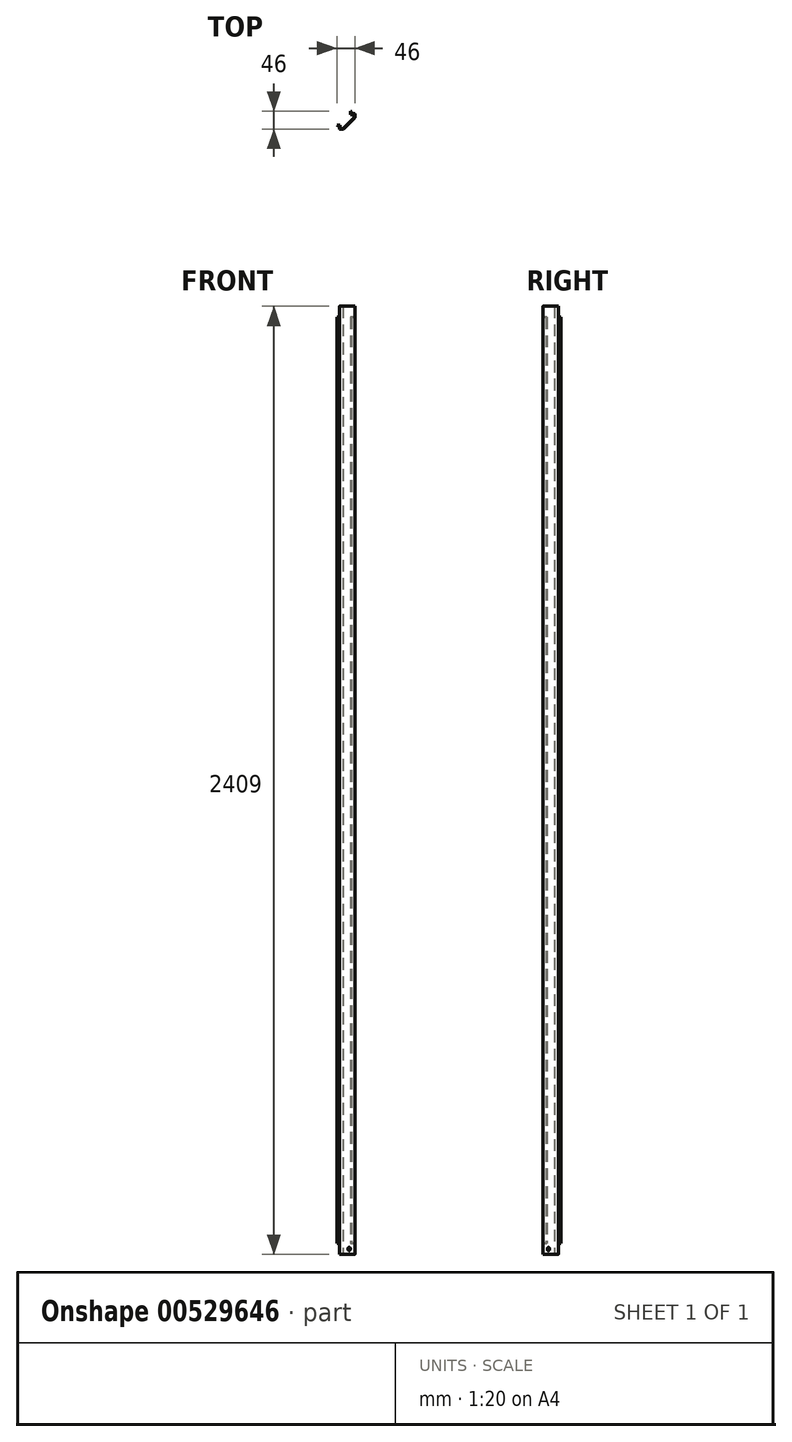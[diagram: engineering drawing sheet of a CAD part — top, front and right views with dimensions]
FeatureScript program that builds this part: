
annotation { "Feature Type Name" : "Feature", "Feature Type Description" : "" }
export const myFeature = defineFeature(function(context is Context, id is Id, definition is map)
    precondition{}
    {
        {
            var Q0;
            Q0=qCreatedBy(makeId("Top.planeOp"),FACE);
            var sketch = newSketch(context, id + "F0", { "sketchPlane" : qUnion([Q0])});
            skLineSegment(sketch, "E0", {"start": v(-68.1, 0) * mm, "end": v(72.16, 0) * mm, "construction": true});
            skLineSegment(sketch, "E1", {"start": v(0, 70.28) * mm, "end": v(0, -61.88) * mm, "construction": true});
            skLineSegment(sketch, "E2.bottom", {"start": v(-19.75, 19.75) * mm, "end": v(19.75, 19.75) * mm, "construction": true});
            skLineSegment(sketch, "E2.top", {"start": v(-19.75, -19.75) * mm, "end": v(19.75, -19.75) * mm, "construction": true});
            skLineSegment(sketch, "E2.left", {"start": v(-19.75, 19.75) * mm, "end": v(-19.75, -19.75) * mm, "construction": true});
            skLineSegment(sketch, "E2.right", {"start": v(19.75, 19.75) * mm, "end": v(19.75, -19.75) * mm, "construction": true});
            skLineSegment(sketch, "E3", {"start": v(-19.75, -19.75) * mm, "end": v(-9.25, -19.75) * mm});
            skLineSegment(sketch, "E4", {"start": v(19.75, 19.75) * mm, "end": v(19.75, 9.25) * mm});
            skLineSegment(sketch, "E5", {"start": v(-9.25, -19.75) * mm, "end": v(19.75, 9.25) * mm});
            skLineSegment(sketch, "E6.0", {"start": v(-19.75, -17.75) * mm, "end": v(-10.08, -17.75) * mm});
            skLineSegment(sketch, "E6.1", {"start": v(-10.08, -17.75) * mm, "end": v(17.75, 10.08) * mm});
            skLineSegment(sketch, "E6.2", {"start": v(17.75, 19.75) * mm, "end": v(17.75, 10.08) * mm});
            skLineSegment(sketch, "E7", {"start": v(-19.75, -19.75) * mm, "end": v(-19.75, -17.75) * mm});
            skLineSegment(sketch, "E8", {"start": v(19.75, 19.75) * mm, "end": v(17.75, 19.75) * mm});
            skSolve(sketch);
        }
        {
            var Q0;
            Q0=qSketchRegion(id+"F0",true);
            extrude(context, id + "F1", {"entities" : qUnion([Q0]), "depth" : 28 * mm});
        }
        {
            var Q0;
            Q0=makeQuery(id+"F1.opExtrude","CAP_FACE",FACE,{"disambiguationData":[OSD([sQuery(id+"F0.wireOp",EDGE,"E3"),sQuery(id+"F0.wireOp",EDGE,"E4"),sQuery(id+"F0.wireOp",EDGE,"E5"),sQuery(id+"F0.wireOp",EDGE,"E6.0"),sQuery(id+"F0.wireOp",EDGE,"E6.1"),sQuery(id+"F0.wireOp",EDGE,"E6.2"),sQuery(id+"F0.wireOp",EDGE,"E7"),sQuery(id+"F0.wireOp",EDGE,"E8")])],"isStart":false});
            var sketch = newSketch(context, id + "F2", { "sketchPlane" : qUnion([Q0])});
            skLineSegment(sketch, "E9.1", {"start": v(-9.25, -19.75) * mm, "end": v(19.75, 9.25) * mm});
            skLineSegment(sketch, "E9.2", {"start": v(19.75, 19.75) * mm, "end": v(19.75, 9.25) * mm});
            skLineSegment(sketch, "E10", {"start": v(19.75, 19.75) * mm, "end": v(11.25, 19.75) * mm});
            skLineSegment(sketch, "E11", {"start": v(17.75, 17.75) * mm, "end": v(17.75, 10.08) * mm});
            skLineSegment(sketch, "E12", {"start": v(17.75, 10.08) * mm, "end": v(16.59, 8.91) * mm});
            skLineSegment(sketch, "E13.left", {"start": v(11.25, 19.75) * mm, "end": v(11.25, 24.25) * mm});
            skLineSegment(sketch, "E14", {"start": v(11.25, 24.25) * mm, "end": v(9.25, 26.25) * mm});
            skLineSegment(sketch, "E15.trimOffspring", {"start": v(16.59, 8.91) * mm, "end": v(-8.91, -16.59) * mm});
            skLineSegment(sketch, "E16.0", {"start": v(9.25, 19.75) * mm, "end": v(9.25, 23.42) * mm});
            skLineSegment(sketch, "E17.0", {"start": v(9.25, 23.42) * mm, "end": v(9.25, 23.42) * mm});
            skLineSegment(sketch, "E18.trimOffspring", {"start": v(9.25, 23.42) * mm, "end": v(9.25, 26.25) * mm});
            skLineSegment(sketch, "E19", {"start": v(0, 0) * mm, "end": v(5.25, -5.25) * mm, "construction": true});
            skLineSegment(sketch, "E20.MirrorCS", {"start": v(-19.75, -9.25) * mm, "end": v(-23.42, -9.25) * mm});
            skLineSegment(sketch, "E21.MirrorCS", {"start": v(-19.75, -11.25) * mm, "end": v(-24.25, -11.25) * mm});
            skLineSegment(sketch, "E22.MirrorCS", {"start": v(-23.42, -9.25) * mm, "end": v(-26.25, -9.25) * mm});
            skLineSegment(sketch, "E23.MirrorCS", {"start": v(-19.75, -19.75) * mm, "end": v(-9.25, -19.75) * mm});
            skLineSegment(sketch, "E24.MirrorCS", {"start": v(-10.08, -17.75) * mm, "end": v(-8.91, -16.59) * mm});
            skLineSegment(sketch, "E25.MirrorCS", {"start": v(-24.25, -11.25) * mm, "end": v(-26.25, -9.25) * mm});
            skLineSegment(sketch, "E26.MirrorCS", {"start": v(-17.75, -17.75) * mm, "end": v(-10.08, -17.75) * mm});
            skLineSegment(sketch, "E27.MirrorCS", {"start": v(-23.42, -9.25) * mm, "end": v(-23.42, -9.25) * mm});
            skLineSegment(sketch, "E28.MirrorCS", {"start": v(-19.75, -19.75) * mm, "end": v(-19.75, -11.25) * mm});
            skLineSegment(sketch, "E29.trimOffspring", {"start": v(-8.91, -16.59) * mm, "end": v(-10.08, -17.75) * mm});
            skLineSegment(sketch, "E30", {"start": v(9.25, 19.75) * mm, "end": v(9.25, 17.75) * mm});
            skLineSegment(sketch, "E31", {"start": v(9.25, 17.75) * mm, "end": v(17.75, 17.75) * mm});
            skLineSegment(sketch, "E32", {"start": v(-19.75, -9.25) * mm, "end": v(-17.75, -9.25) * mm});
            skLineSegment(sketch, "E33", {"start": v(-17.75, -9.25) * mm, "end": v(-17.75, -17.75) * mm});
            skSolve(sketch);
        }
        {
            var Q0;
            Q0=qSketchRegion(id+"F2",true);
            extrude(context, id + "F3", {"entities" : qUnion([Q0]), "operationType" : NewBodyOperationType.ADD, "depth" : 2353 * mm, "offsetDistance" : 25 * mm});
        }
        {
            var Q0;
            Q0=makeQuery(id+"F3.opExtrude","CAP_FACE",FACE,{"disambiguationData":[OSD([sQuery(id+"F2.wireOp",EDGE,"E9.1"),sQuery(id+"F2.wireOp",EDGE,"E9.2"),sQuery(id+"F2.wireOp",EDGE,"E10"),sQuery(id+"F2.wireOp",EDGE,"E11"),sQuery(id+"F2.wireOp",EDGE,"E12"),sQuery(id+"F2.wireOp",EDGE,"E13.left"),sQuery(id+"F2.wireOp",EDGE,"E14"),sQuery(id+"F2.wireOp",EDGE,"E15.trimOffspring"),sQuery(id+"F2.wireOp",EDGE,"E16.0"),sQuery(id+"F2.wireOp",EDGE,"E17.0"),sQuery(id+"F2.wireOp",EDGE,"E18.trimOffspring"),sQuery(id+"F2.wireOp",EDGE,"E20.MirrorCS"),sQuery(id+"F2.wireOp",EDGE,"E21.MirrorCS"),sQuery(id+"F2.wireOp",EDGE,"E22.MirrorCS"),sQuery(id+"F2.wireOp",EDGE,"E23.MirrorCS"),sQuery(id+"F2.wireOp",EDGE,"E25.MirrorCS"),sQuery(id+"F2.wireOp",EDGE,"E26.MirrorCS"),sQuery(id+"F2.wireOp",EDGE,"E27.MirrorCS"),sQuery(id+"F2.wireOp",EDGE,"E28.MirrorCS"),sQuery(id+"F2.wireOp",EDGE,"E29.trimOffspring"),sQuery(id+"F2.wireOp",EDGE,"E30"),sQuery(id+"F2.wireOp",EDGE,"E31"),sQuery(id+"F2.wireOp",EDGE,"E32"),sQuery(id+"F2.wireOp",EDGE,"E33")])],"isStart":false});
            var sketch = newSketch(context, id + "F4", { "sketchPlane" : qUnion([Q0])});
            skLineSegment(sketch, "E34.0.0", {"start": v(19.75, 19.75) * mm, "end": v(19.75, 9.25) * mm});
            skLineSegment(sketch, "E34.0.1", {"start": v(19.75, 9.25) * mm, "end": v(-9.25, -19.75) * mm});
            skLineSegment(sketch, "E34.0.2", {"start": v(-9.25, -19.75) * mm, "end": v(-19.75, -19.75) * mm});
            skLineSegment(sketch, "E34.0.3", {"start": v(-19.75, -19.75) * mm, "end": v(-19.75, -17.75) * mm});
            skLineSegment(sketch, "E34.0.4", {"start": v(-19.75, -17.75) * mm, "end": v(-10.08, -17.75) * mm});
            skLineSegment(sketch, "E34.0.5", {"start": v(-10.08, -17.75) * mm, "end": v(17.75, 10.08) * mm});
            skLineSegment(sketch, "E34.0.6", {"start": v(17.75, 10.08) * mm, "end": v(17.75, 19.75) * mm});
            skLineSegment(sketch, "E34.0.7", {"start": v(17.75, 19.75) * mm, "end": v(19.75, 19.75) * mm});
            skSolve(sketch);
        }
        {
            var Q0;
            Q0=qSketchRegion(id+"F4",true);
            extrude(context, id + "F5", {"entities" : qUnion([Q0]), "operationType" : NewBodyOperationType.ADD, "depth" : 28 * mm});
        }
        {
            var Q0;
            Q0=makeQuery(id+"F5.boolean.opBoolean","MERGE",EDGE,{"derivedFrom":[makeQuery(id+"F3.boolean.opBoolean","MERGE",EDGE,{"derivedFrom":[makeQuery(id+"F1.opExtrude","SWEPT_EDGE",EDGE,{"disambiguationData":[OSD([sQuery(id+"F0.wireOp",EDGE,"E4"),sQuery(id+"F0.wireOp",EDGE,"E5")])]}),makeQuery(id+"F3.opExtrude","SWEPT_EDGE",EDGE,{"disambiguationData":[OSD([sQuery(id+"F2.wireOp",EDGE,"E9.1"),sQuery(id+"F2.wireOp",EDGE,"E9.2")])]})]}),makeQuery(id+"F5.opExtrude","SWEPT_EDGE",EDGE,{"disambiguationData":[OSD([sQuery(id+"F4.wireOp",EDGE,"E34.0.0"),sQuery(id+"F4.wireOp",EDGE,"E34.0.1")])]})]});
            var Q1;
            Q1=makeQuery(id+"F5.boolean.opBoolean","MERGE",EDGE,{"derivedFrom":[makeQuery(id+"F3.boolean.opBoolean","MERGE",EDGE,{"derivedFrom":[makeQuery(id+"F1.opExtrude","SWEPT_EDGE",EDGE,{"disambiguationData":[OSD([sQuery(id+"F0.wireOp",EDGE,"E3"),sQuery(id+"F0.wireOp",EDGE,"E5")])]}),makeQuery(id+"F3.opExtrude","SWEPT_EDGE",EDGE,{"disambiguationData":[OSD([sQuery(id+"F2.wireOp",EDGE,"E9.1"),sQuery(id+"F2.wireOp",EDGE,"E23.MirrorCS")])]})]}),makeQuery(id+"F5.opExtrude","SWEPT_EDGE",EDGE,{"disambiguationData":[OSD([sQuery(id+"F4.wireOp",EDGE,"E34.0.1"),sQuery(id+"F4.wireOp",EDGE,"E34.0.2")])]})]});
            fillet(context, id + "F6", {"entities" : qUnion([Q0, Q1]), "radius" : 2 * mm, "tangentPropagation" : true, "allowEdgeOverflow" : false});
        }
        {
            var Q0;
            Q0=makeQuery(id+"F5.boolean.opBoolean","MERGE",EDGE,{"derivedFrom":[makeQuery(id+"F3.boolean.opBoolean","MERGE",EDGE,{"derivedFrom":[makeQuery(id+"F1.opExtrude","SWEPT_EDGE",EDGE,{"disambiguationData":[OSD([sQuery(id+"F0.wireOp",EDGE,"E3"),sQuery(id+"F0.wireOp",EDGE,"E7")])]}),makeQuery(id+"F3.opExtrude","SWEPT_EDGE",EDGE,{"disambiguationData":[OSD([sQuery(id+"F2.wireOp",EDGE,"E23.MirrorCS"),sQuery(id+"F2.wireOp",EDGE,"E28.MirrorCS")])]})]}),makeQuery(id+"F5.opExtrude","SWEPT_EDGE",EDGE,{"disambiguationData":[OSD([sQuery(id+"F4.wireOp",EDGE,"E34.0.2"),sQuery(id+"F4.wireOp",EDGE,"E34.0.3")])]})]});
            var Q1;
            Q1=makeQuery(id+"F5.boolean.opBoolean","MERGE",EDGE,{"derivedFrom":[makeQuery(id+"F3.boolean.opBoolean","MERGE",EDGE,{"derivedFrom":[makeQuery(id+"F1.opExtrude","SWEPT_EDGE",EDGE,{"disambiguationData":[OSD([sQuery(id+"F0.wireOp",EDGE,"E4"),sQuery(id+"F0.wireOp",EDGE,"E8")])]}),makeQuery(id+"F3.opExtrude","SWEPT_EDGE",EDGE,{"disambiguationData":[OSD([sQuery(id+"F2.wireOp",EDGE,"E9.2"),sQuery(id+"F2.wireOp",EDGE,"E10")])]})]}),makeQuery(id+"F5.opExtrude","SWEPT_EDGE",EDGE,{"disambiguationData":[OSD([sQuery(id+"F4.wireOp",EDGE,"E34.0.0"),sQuery(id+"F4.wireOp",EDGE,"E34.0.7")])]})]});
            fillet(context, id + "F7", {"entities" : qUnion([Q0, Q1]), "radius" : 1 * mm, "tangentPropagation" : true, "allowEdgeOverflow" : false});
        }
        {
            var Q0;
            Q0=makeQuery(id+"F5.boolean.opBoolean","MERGE",FACE,{"derivedFrom":[makeQuery(id+"F3.boolean.opBoolean","MERGE",FACE,{"derivedFrom":[makeQuery(id+"F1.opExtrude","SWEPT_FACE",FACE,{"disambiguationData":[OSD([sQuery(id+"F0.wireOp",EDGE,"E6.1")])]}),makeQuery(id+"F3.opExtrude","SWEPT_FACE",FACE,{"disambiguationData":[OSD([sQuery(id+"F2.wireOp",EDGE,"E12"),sQuery(id+"F2.wireOp",EDGE,"E15.trimOffspring"),sQuery(id+"F2.wireOp",EDGE,"E29.trimOffspring")])]})]}),makeQuery(id+"F5.opExtrude","SWEPT_FACE",FACE,{"disambiguationData":[OSD([sQuery(id+"F4.wireOp",EDGE,"E34.0.5")])]})]});
            var sketch = newSketch(context, id + "F8", { "sketchPlane" : qUnion([Q0])});
            skLineSegment(sketch, "E35", {"start": v(-26.52, 28) * mm, "end": v(26.52, 28) * mm, "construction": true});
            skLineSegment(sketch, "E36", {"start": v(0, 28) * mm, "end": v(0, 0) * mm, "construction": true});
            skCircle(sketch, "E37", {"center": v(0, 14) * mm, "radius": 4.25 * mm});
            skSolve(sketch);
        }
        {
            var Q0;
            Q0 = qSketchRegion(id + "F8", true);
            extrude(context, id + "F9", {"entities" : qUnion([Q0]), "operationType" : NewBodyOperationType.REMOVE, "oppositeDirection" : true, "depth" : 25 * mm, "offsetDistance" : 25 * mm});
        }
    });
